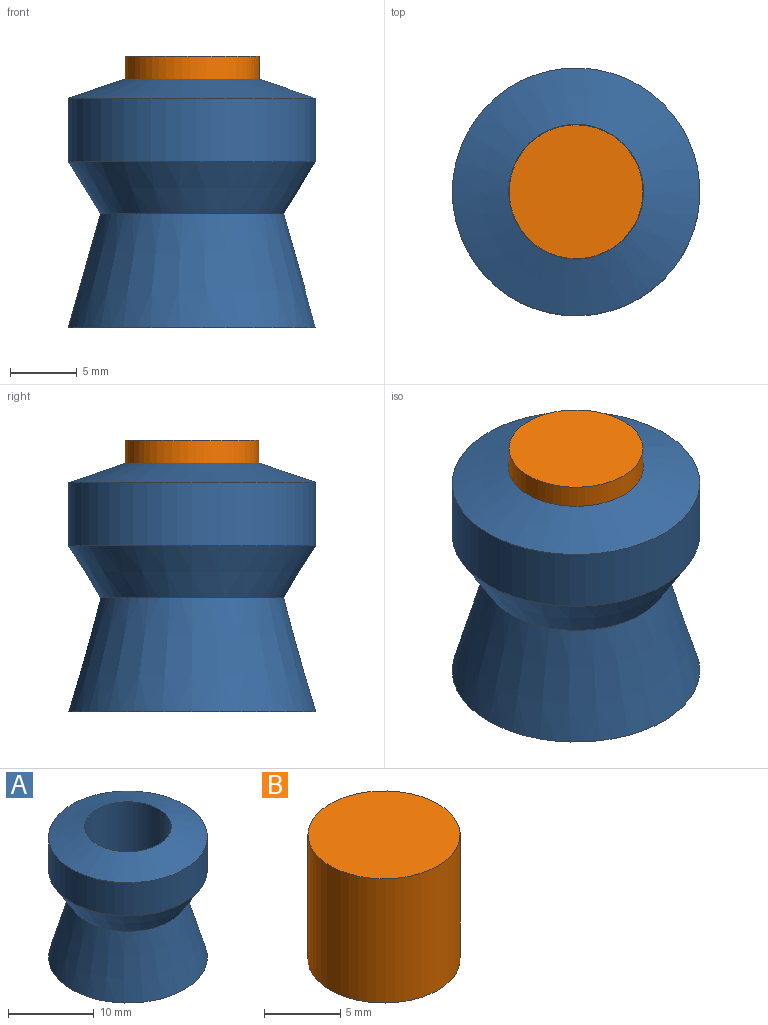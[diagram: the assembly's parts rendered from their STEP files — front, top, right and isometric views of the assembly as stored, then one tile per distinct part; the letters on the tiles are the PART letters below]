
ASSEMBLY  parts=2 mates=1
PART A: 7 faces, bbox 18.5x18.5x18.6 mm
  f0: cylinder r=5.04mm len=10.09mm, axis (0,0,-1), area 262.5mm2, adj f1,f6
  f1: plane 10.09x10.09mm, normal (0,0,1), area 79.9mm2, adj f0
  f2: plane 18.51x18.51mm, normal (0,0,-1), area 269.1mm2, adj f3
  f3: cone r=9.25mm half-angle=15.8deg, axis (0,0,-1), area 448mm2, adj f2,f4
  f4: cone r=9.25mm half-angle=31.7deg, axis (0,0,1), area 232.5mm2, adj f3,f5
  f5: cylinder r=9.25mm len=18.51mm, axis (0,0,-1), area 274.9mm2, adj f4,f6
  f6: cone r=5.04mm half-angle=71.1deg, axis (0,0,-1), area 199.9mm2, adj f0,f5
PART B: 3 faces, bbox 10x10x10 mm
  f0: plane 10x10mm, normal (0,0,-1), area 78.5mm2, adj f1
  f1: cylinder r=5mm len=10mm, axis (0,0,1), area 314.2mm2, adj f0,f2
  f2: plane 10x10mm, normal (0,0,1), area 78.5mm2, adj f1
PLACE A t=(0,0,-5)mm
PLACE B t=(-40.41,0,5.32)mm
MATE fastened B.f1 <-> A.f0  axis (0,0,-1) through (0,0,5.32)mm
